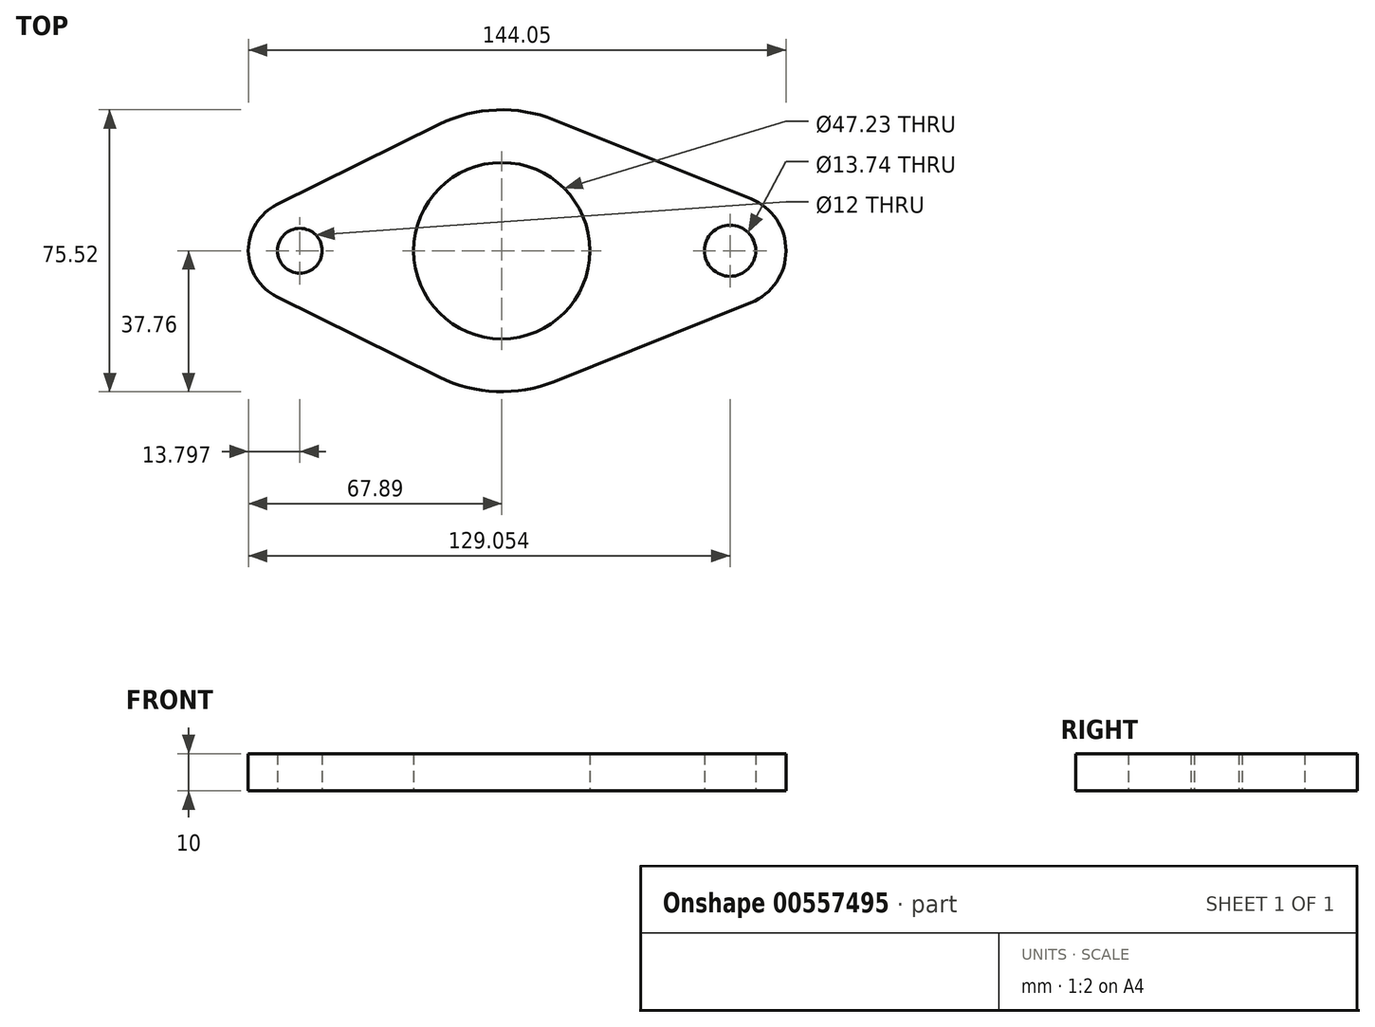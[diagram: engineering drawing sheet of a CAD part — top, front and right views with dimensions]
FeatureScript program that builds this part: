
annotation { "Feature Type Name" : "Feature", "Feature Type Description" : "" }
export const myFeature = defineFeature(function(context is Context, id is Id, definition is map)
    precondition{}
    {
        {
            var Q0;
            Q0=qCreatedBy(makeId("Top.planeOp"),FACE);
            var sketch = newSketch(context, id + "F0", { "sketchPlane" : qUnion([Q0])});
            skCircle(sketch, "E0", {"center": v(0, 0) * mm, "radius": 23.62 * mm});
            skArc(sketch, "E1", {"start": v(-16.73, -33.86) * mm, "mid": v(-1.46, -37.74) * mm, "end": v(14.05, -35.05) * mm});
            skCircle(sketch, "E2", {"center": v(61.16, 0) * mm, "radius": 6.87 * mm});
            skArc(sketch, "E3", {"start": v(-60.2, 12.37) * mm, "mid": v(-67.9, 0) * mm, "end": v(-60.2, -12.37) * mm});
            skArc(sketch, "E4", {"start": v(66.75, -13.92) * mm, "mid": v(76.16, 0) * mm, "end": v(66.75, 13.92) * mm});
            skLineSegment(sketch, "E5", {"start": v(-60.2, 12.37) * mm, "end": v(-16.73, 33.86) * mm});
            skCircle(sketch, "E6", {"center": v(-54.1, 0) * mm, "radius": 6 * mm});
            skLineSegment(sketch, "E7", {"start": v(14.05, 35.05) * mm, "end": v(66.75, 13.92) * mm});
            skLineSegment(sketch, "E8", {"start": v(-60.2, -12.37) * mm, "end": v(-16.73, -33.86) * mm});
            skLineSegment(sketch, "E9", {"start": v(14.05, -35.05) * mm, "end": v(66.75, -13.92) * mm});
            skArc(sketch, "E10.trimOffspring", {"start": v(14.05, 35.05) * mm, "mid": v(-1.46, 37.74) * mm, "end": v(-16.73, 33.86) * mm});
            skSolve(sketch);
        }
        {
            var Q0;
            Q0 = qSketchRegion(id + "F0", true);
            extrude(context, id + "F1", {"entities" : qUnion([Q0]), "depth" : 10 * mm, "offsetDistance" : 25 * mm});
        }
    });
